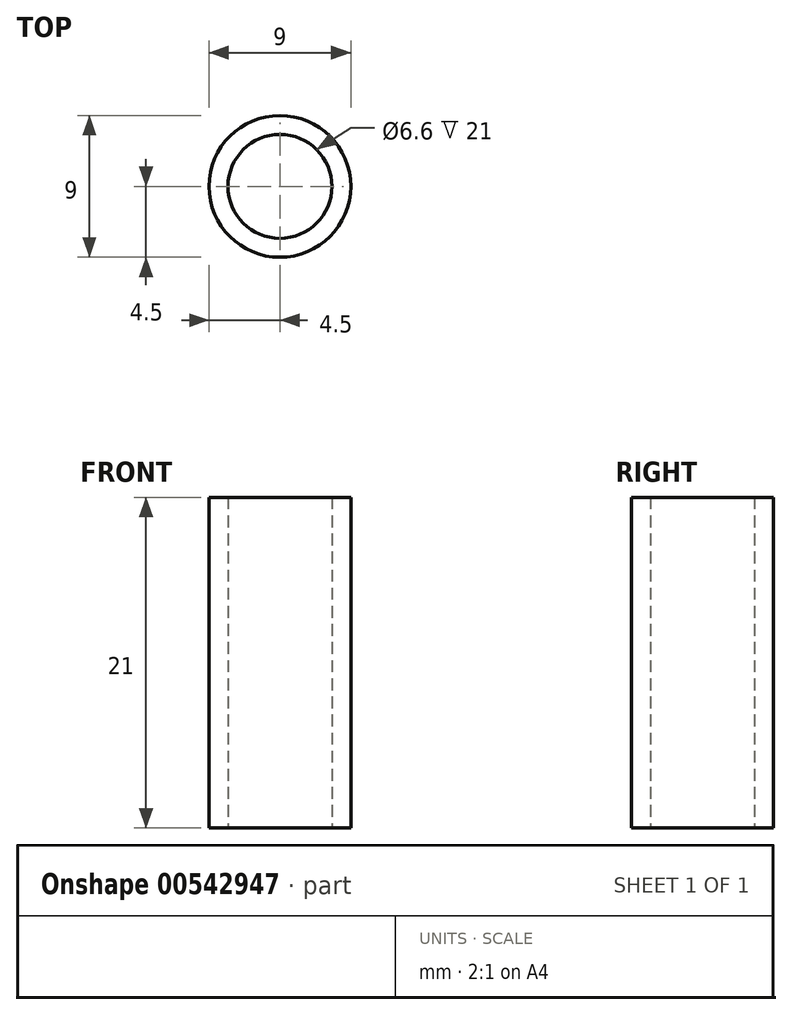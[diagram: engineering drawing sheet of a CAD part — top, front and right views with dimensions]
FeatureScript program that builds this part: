
annotation { "Feature Type Name" : "Feature", "Feature Type Description" : "" }
export const myFeature = defineFeature(function(context is Context, id is Id, definition is map)
    precondition{}
    {
        {
            var Q0;
            Q0=qCreatedBy(makeId("Top.planeOp"),FACE);
            var sketch = newSketch(context, id + "F0", { "sketchPlane" : qUnion([Q0])});
            skCircle(sketch, "E0", {"center": v(0, 0) * mm, "radius": 3.3 * mm});
            skCircle(sketch, "E1", {"center": v(0, 0) * mm, "radius": 4.5 * mm});
            skSolve(sketch);
        }
        {
            var Q0;
            Q0=makeQuery(id+"F0.imprint","IMPRINT",FACE,{"disambiguationData":[TD([[makeQuery(id+"F0.imprint","IMPRINT",EDGE,{"derivedFrom":sQuery(id+"F0.wireOp",EDGE,"E0")}),-1.0]])]});
            extrude(context, id + "F1", {"entities" : qUnion([Q0]), "depth" : 21 * mm, "offsetDistance" : 25 * mm});
        }
    });
